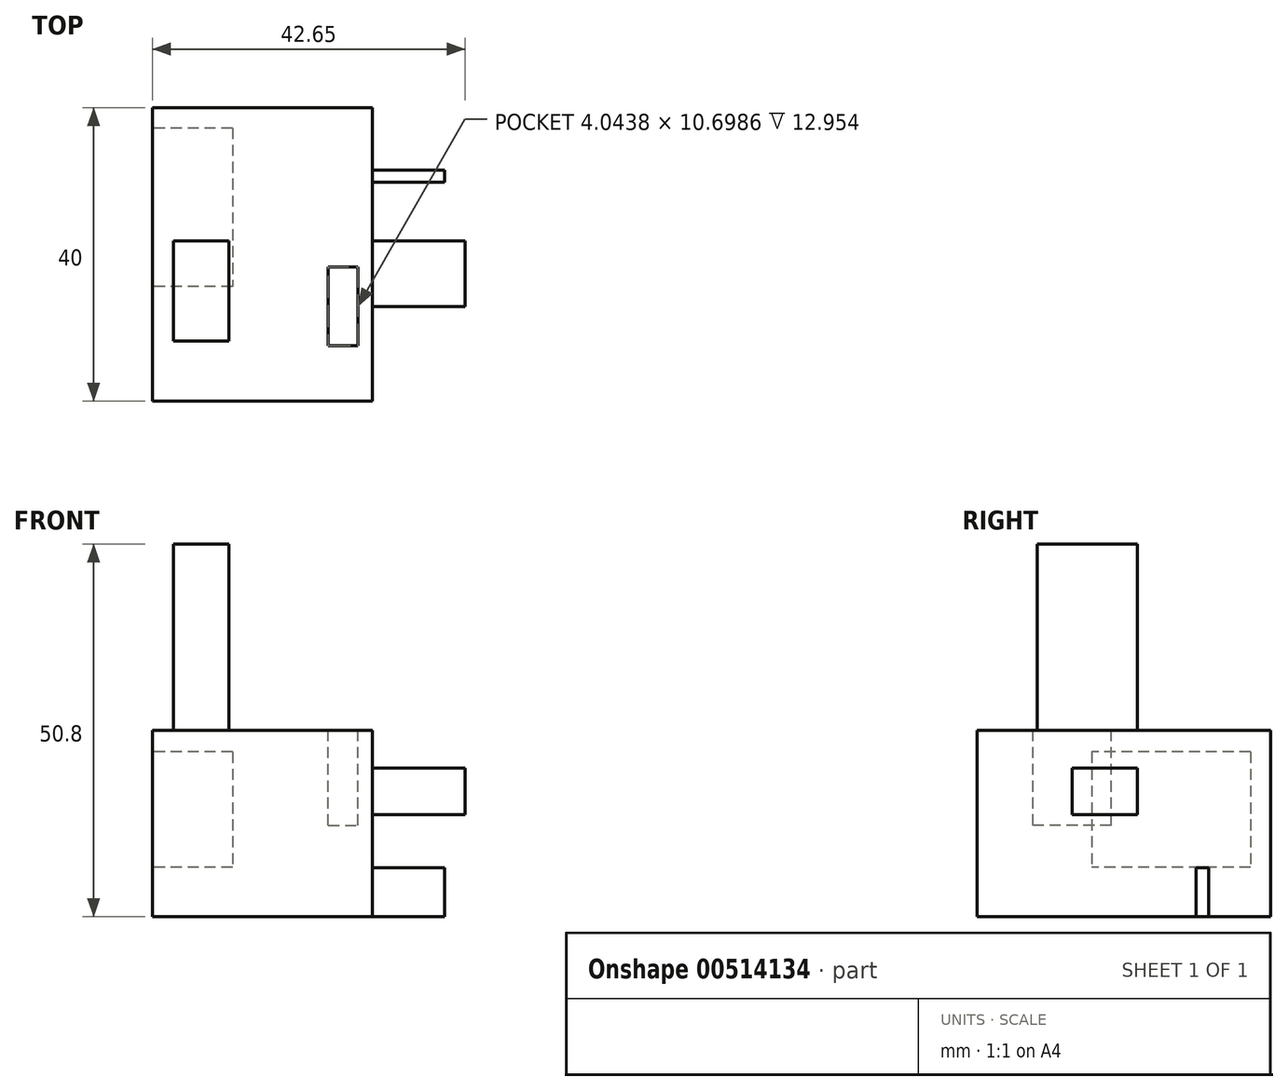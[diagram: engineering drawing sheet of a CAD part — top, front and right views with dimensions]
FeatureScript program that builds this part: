
annotation { "Feature Type Name" : "Feature", "Feature Type Description" : "" }
export const myFeature = defineFeature(function(context is Context, id is Id, definition is map)
    precondition{}
    {
        {
            var Q0;
            Q0=qCreatedBy(makeId("Top.planeOp"),FACE);
            var sketch = newSketch(context, id + "F0", { "sketchPlane" : qUnion([Q0])});
            skLineSegment(sketch, "E0.bottom", {"start": v(-14.44, -21.84) * mm, "end": v(15.56, -21.84) * mm});
            skLineSegment(sketch, "E0.top", {"start": v(-14.44, 18.16) * mm, "end": v(15.56, 18.16) * mm});
            skLineSegment(sketch, "E0.left", {"start": v(-14.44, -21.84) * mm, "end": v(-14.44, 18.16) * mm});
            skLineSegment(sketch, "E0.right", {"start": v(15.56, -21.84) * mm, "end": v(15.56, 18.16) * mm});
            skSolve(sketch);
        }
        {
            var Q0;
            Q0 = qSketchRegion(id + "F0", true);
            extrude(context, id + "F1", {"entities" : qUnion([Q0]), "depth" : 25.4 * mm});
        }
        {
            var Q0;
            Q0=makeQuery(id+"F1.opExtrude","CAP_FACE",FACE,{"disambiguationData":[OSD([sQuery(id+"F0.wireOp",EDGE,"E0.bottom"),sQuery(id+"F0.wireOp",EDGE,"E0.top"),sQuery(id+"F0.wireOp",EDGE,"E0.left"),sQuery(id+"F0.wireOp",EDGE,"E0.right")])],"isStart":false});
            var sketch = newSketch(context, id + "F2", { "sketchPlane" : qUnion([Q0])});
            skSolve(sketch);
        }
        {
            var Q0;
            Q0=makeQuery(id+"F2.imprint","IMPRINT",FACE,{"disambiguationData":[TD([[makeQuery(id+"F2.imprint","IMPRINT",EDGE,{"derivedFrom":makeQuery(id+"F1.opExtrude","CAP_EDGE",EDGE,{"disambiguationData":[OSD([sQuery(id+"F0.wireOp",EDGE,"E0.bottom")])],"isStart":false})}),1.0]])]});
            var sketch = newSketch(context, id + "F3", { "sketchPlane" : qUnion([Q0])});
            skLineSegment(sketch, "E1.bottom", {"start": v(-4.01, 0) * mm, "end": v(-11.55, 0) * mm});
            skLineSegment(sketch, "E1.top", {"start": v(-4.01, -13.68) * mm, "end": v(-11.55, -13.68) * mm});
            skLineSegment(sketch, "E1.left", {"start": v(-4.01, 0) * mm, "end": v(-4.01, -13.68) * mm});
            skLineSegment(sketch, "E1.right", {"start": v(-11.55, 0) * mm, "end": v(-11.55, -13.68) * mm});
            skSolve(sketch);
        }
        {
            var Q0;
            Q0 = qSketchRegion(id + "F3", true);
            extrude(context, id + "F4", {"entities" : qUnion([Q0]), "operationType" : NewBodyOperationType.ADD, "depth" : 25.4 * mm});
        }
        {
            var Q0;
            Q0=makeQuery(id+"F2.imprint","IMPRINT",FACE,{"disambiguationData":[TD([[makeQuery(id+"F2.imprint","IMPRINT",EDGE,{"derivedFrom":makeQuery(id+"F1.opExtrude","CAP_EDGE",EDGE,{"disambiguationData":[OSD([sQuery(id+"F0.wireOp",EDGE,"E0.bottom")])],"isStart":false})}),1.0]])]});
            var sketch = newSketch(context, id + "F5", { "sketchPlane" : qUnion([Q0])});
            skLineSegment(sketch, "E2.bottom", {"start": v(9.55, -3.58) * mm, "end": v(13.6, -3.58) * mm});
            skLineSegment(sketch, "E2.top", {"start": v(9.55, -14.28) * mm, "end": v(13.6, -14.28) * mm});
            skLineSegment(sketch, "E2.left", {"start": v(9.55, -3.58) * mm, "end": v(9.55, -14.28) * mm});
            skLineSegment(sketch, "E2.right", {"start": v(13.6, -3.58) * mm, "end": v(13.6, -14.28) * mm});
            skSolve(sketch);
        }
        {
            var Q0;
            Q0 = qSketchRegion(id + "F5", true);
            extrude(context, id + "F6", {"entities" : qUnion([Q0]), "operationType" : NewBodyOperationType.REMOVE, "oppositeDirection" : true, "depth" : 12.95 * mm});
        }
        {
            var Q0;
            Q0=qCreatedBy(makeId("Right.planeOp"),FACE);
            var sketch = newSketch(context, id + "F7", { "sketchPlane" : qUnion([Q0])});
            skLineSegment(sketch, "E3.bottom", {"start": v(7.98, 6.7) * mm, "end": v(9.66, 6.7) * mm});
            skLineSegment(sketch, "E3.top", {"start": v(7.98, 0) * mm, "end": v(9.66, 0) * mm});
            skLineSegment(sketch, "E3.left", {"start": v(7.98, 6.7) * mm, "end": v(7.98, 0) * mm});
            skLineSegment(sketch, "E3.right", {"start": v(9.66, 6.7) * mm, "end": v(9.66, 0) * mm});
            skSolve(sketch);
        }
        {
            var Q0;
            Q0 = qSketchRegion(id + "F7", true);
            extrude(context, id + "F8", {"entities" : qUnion([Q0]), "operationType" : NewBodyOperationType.ADD, "depth" : 25.4 * mm});
        }
        {
            var Q0;
            Q0=makeQuery(id+"F1.opExtrude","SWEPT_FACE",FACE,{"disambiguationData":[OSD([sQuery(id+"F0.wireOp",EDGE,"E0.left")])]});
            var sketch = newSketch(context, id + "F9", { "sketchPlane" : qUnion([Q0])});
            skLineSegment(sketch, "E4.bottom", {"start": v(-15.4, 22.46) * mm, "end": v(6.24, 22.46) * mm});
            skLineSegment(sketch, "E4.top", {"start": v(-15.4, 6.75) * mm, "end": v(6.24, 6.75) * mm});
            skLineSegment(sketch, "E4.left", {"start": v(-15.4, 22.46) * mm, "end": v(-15.4, 6.75) * mm});
            skLineSegment(sketch, "E4.right", {"start": v(6.24, 22.46) * mm, "end": v(6.24, 6.75) * mm});
            skSolve(sketch);
        }
        {
            var Q0;
            Q0 = qSketchRegion(id + "F9", true);
            extrude(context, id + "F10", {"entities" : qUnion([Q0]), "operationType" : NewBodyOperationType.REMOVE, "oppositeDirection" : true, "depth" : 10.92 * mm});
        }
        {
            var Q0;
            Q0=makeQuery(id+"F1.opExtrude","SWEPT_FACE",FACE,{"disambiguationData":[OSD([sQuery(id+"F0.wireOp",EDGE,"E0.right")])]});
            var sketch = newSketch(context, id + "F11", { "sketchPlane" : qUnion([Q0])});
            skLineSegment(sketch, "E5.bottom", {"start": v(-8.94, 13.94) * mm, "end": v(0, 13.94) * mm});
            skLineSegment(sketch, "E5.top", {"start": v(-8.94, 20.23) * mm, "end": v(0, 20.23) * mm});
            skLineSegment(sketch, "E5.left", {"start": v(-8.94, 13.94) * mm, "end": v(-8.94, 20.23) * mm});
            skLineSegment(sketch, "E5.right", {"start": v(0, 13.94) * mm, "end": v(0, 20.23) * mm});
            skSolve(sketch);
        }
        {
            var Q0;
            Q0 = qSketchRegion(id + "F11", true);
            extrude(context, id + "F12", {"entities" : qUnion([Q0]), "operationType" : NewBodyOperationType.ADD, "depth" : 12.65 * mm});
        }
    });
